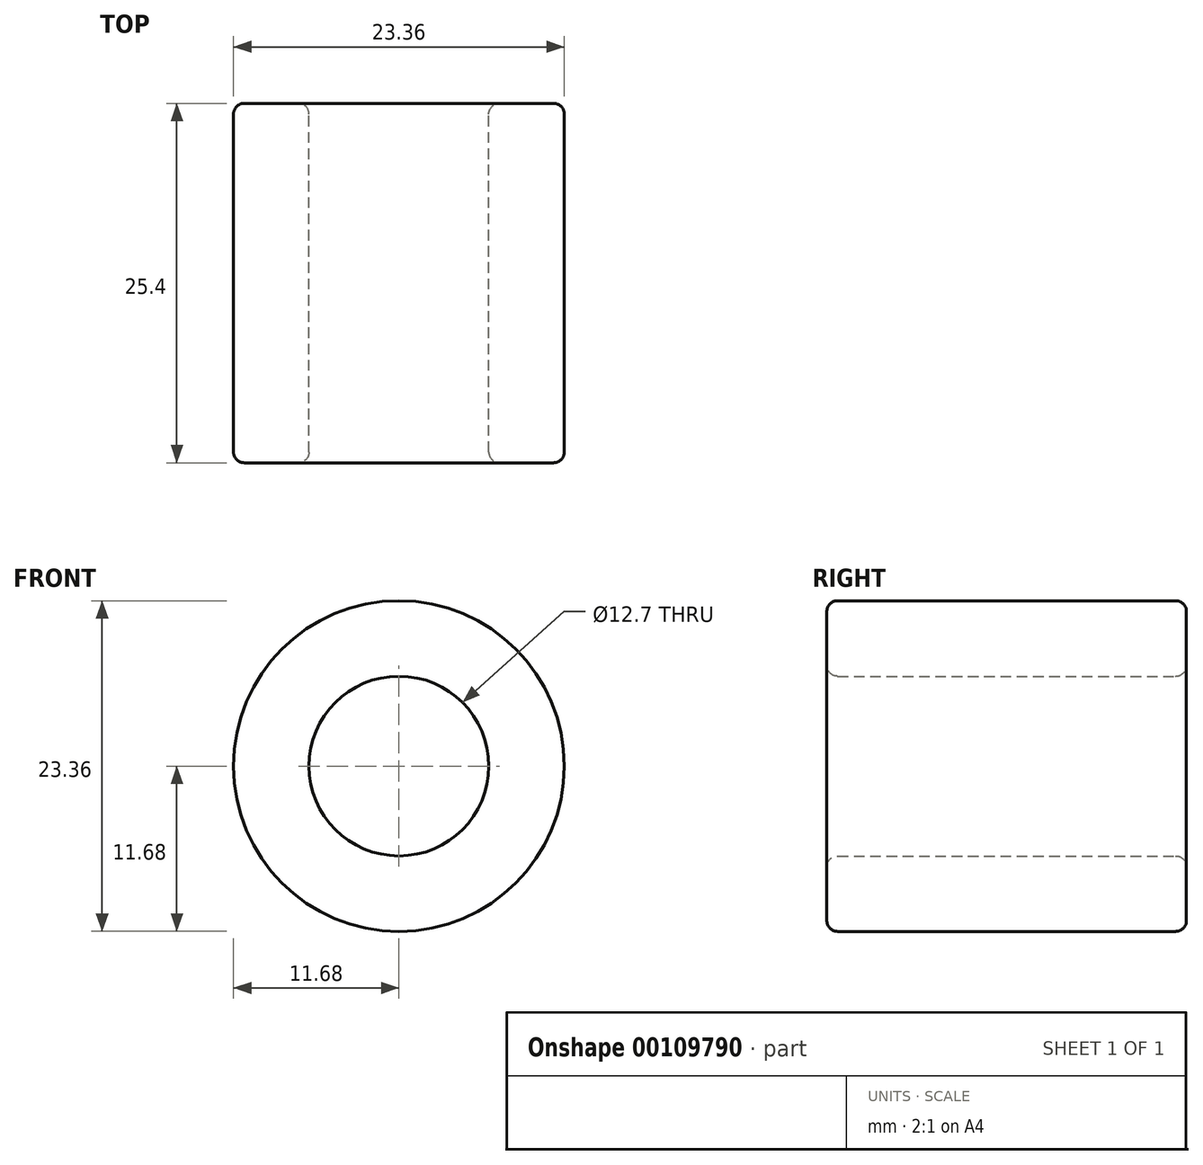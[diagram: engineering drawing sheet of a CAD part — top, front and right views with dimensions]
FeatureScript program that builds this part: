
annotation { "Feature Type Name" : "Feature", "Feature Type Description" : "" }
export const myFeature = defineFeature(function(context is Context, id is Id, definition is map)
    precondition{}
    {
        {
            var Q0;
            Q0=qCreatedBy(makeId("Front.planeOp"),FACE);
            var sketch = newSketch(context, id + "F0", { "sketchPlane" : qUnion([Q0])});
            skCircle(sketch, "E0", {"center": v(0, 0) * mm, "radius": 11.68 * mm});
            skCircle(sketch, "E1", {"center": v(0, 0) * mm, "radius": 6.35 * mm});
            skSolve(sketch);
        }
        {
            var Q0;
            Q0 = qSketchRegion(id + "F0", true);
            extrude(context, id + "F1", {"entities" : qUnion([Q0]), "depth" : 25.4 * mm});
        }
        {
            var Q0;
            Q0=makeQuery(id+"F1.opExtrude","CAP_EDGE",EDGE,{"disambiguationData":[OSD([sQuery(id+"F0.wireOp",EDGE,"E0")])],"isStart":false});
            var Q1;
            Q1=makeQuery(id+"F1.opExtrude","CAP_EDGE",EDGE,{"disambiguationData":[OSD([sQuery(id+"F0.wireOp",EDGE,"E1")])],"isStart":false});
            var Q2;
            Q2=makeQuery(id+"F1.opExtrude","CAP_EDGE",EDGE,{"disambiguationData":[OSD([sQuery(id+"F0.wireOp",EDGE,"E1")])],"isStart":true});
            var Q3;
            Q3=makeQuery(id+"F1.opExtrude","CAP_EDGE",EDGE,{"disambiguationData":[OSD([sQuery(id+"F0.wireOp",EDGE,"E0")])],"isStart":true});
            fillet(context, id + "F2", {"entities" : qUnion([Q0, Q1, Q2, Q3]), "radius" : 0.76 * mm, "tangentPropagation" : true, "allowEdgeOverflow" : false});
        }
    });
